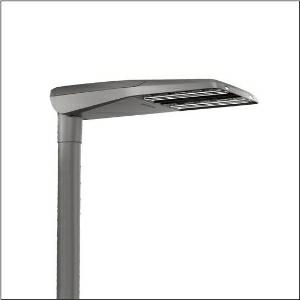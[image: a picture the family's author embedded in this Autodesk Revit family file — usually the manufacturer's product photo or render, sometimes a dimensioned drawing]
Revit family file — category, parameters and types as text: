
# Revit family: streetlight_sl_11_iq_midi___pc-r_5xc3f41f08me_b4e0
name_source: partatom
category: Lighting Fixtures
units: mm (PartAtom-declared; Revit-internal decimal feet)

## family parameters
Cut with Voids When Loaded = No
Host = Face
Light Source = No
Part Type = Normal
Room Calculation Point = No
Round Connector Dimension = Use Diameter
Shared = No

## types (1)
- --- (1 x LED, 16220 lm, 124.7 W, 4000K)
    Apparent Load = 125 VA
    CIE Flux Codes = 37 73 96 100 100
    Color Rendering = 70
    Color Temperature = 4000K
    Default Elevation = 1800 mm
    Description = Streetlight SL 11 iQ midi, mast luminaire, primary light control with 3 zone facetted reflector, of plastic, silver coated, highly specular, primary optical cover: cover, of PMMA, transparent, light distribution: PC-R, light emission: direct distribution, primary light characteristic: asymmetric, installation type: post-top, side-entry, LED, High Power LED, rated luminous flux: 16.220lm, luminous efficacy: 130lm/W, light colour: 740, colour temperature: 4000K, control: Street-Remote, optimised constant luminous flux control (CLO 2.0), Desk-Remote (wireless, voltage-free reading and setting of iQ features in the workshop via application-optimized NFC function/RFID function), Light-Fading, Smart-Wire, Night-Set, Lumen-Switch, Temp-Guard, Auto-Match, with cable H07RN-F 5x 1.5mm², mains connection: 220..240V, AC, 50/60Hz, connection cable pre-assembled, cable length: 12,5m, start of lifetime: 125W, end of lifetime: 132W, reduction: 57W, luminaire housing, of diecast aluminium, powder-coated, Siteco® metallic grey (DB 702S), length: 780mm, width: 376mm, height: 118mm, spigot size: 60/76mm (post-top) and 42/60/76mm (side-entry), mast flange for spigot size: 42mm: 5XC10008XM4, 60mm: 5XC10008XM2, 76/60mm: 5XC10108XM1, equipment: Power, protection rating (complete): IP66, insulation class (complete): insulation class II (safety insulation), certification: CE, ENEC, VDE, impact resistance: IK09, permissible operating ambient temperature for outdoor applications: -25..+50°C, standard-compliant lighting for roads and squares, packaging unit: 1 piece

Light Distribution: PC-R
    Height = 118 mm
    Lamp = 1 x LED
    Lamp Light Flux = 16220 lm
    Lamp Power = 124.7 W
    Lamp count = 1
    Length = 780 mm
    Luminous efficacy = 130 lm/W
    Manufacturer = Siteco
    ModVariant = No
    Model = 5XC3F41F08ME
    Number of Poles = 1
    OnlyDefault = Yes
    Power Factor = 1
    Product Name = Streetlight SL 11 iQ midi | PC-R
    Product group = mast luminaire | pylon top
    ProductGroupID = 6100
    Protection Class = Protection class II
    Protection Degree = IP 66
    RLX_Detail_Level = 1
    RlxData = <blob elided: 74205 chars, md5=f1b53438>
    Socket = socket
    Standby Power = 0 W
    System Light Flux = 16220 lm
    System Power = 125 W
    Type Comments = factory setting: luminous flux: 100 % | dim-lin: 254 | 557 mA
    Type Image = l_1005960.jpg
    URL = http://relux.com
    VarID = @adj_117703
    Voltage = 0 V
    Weight = 0.00 kg
    Width = 376 mm

## geometry (parser evidence)
native form markers: Blend x4, Sweep x10
no freeform markers — native parametric forms only
